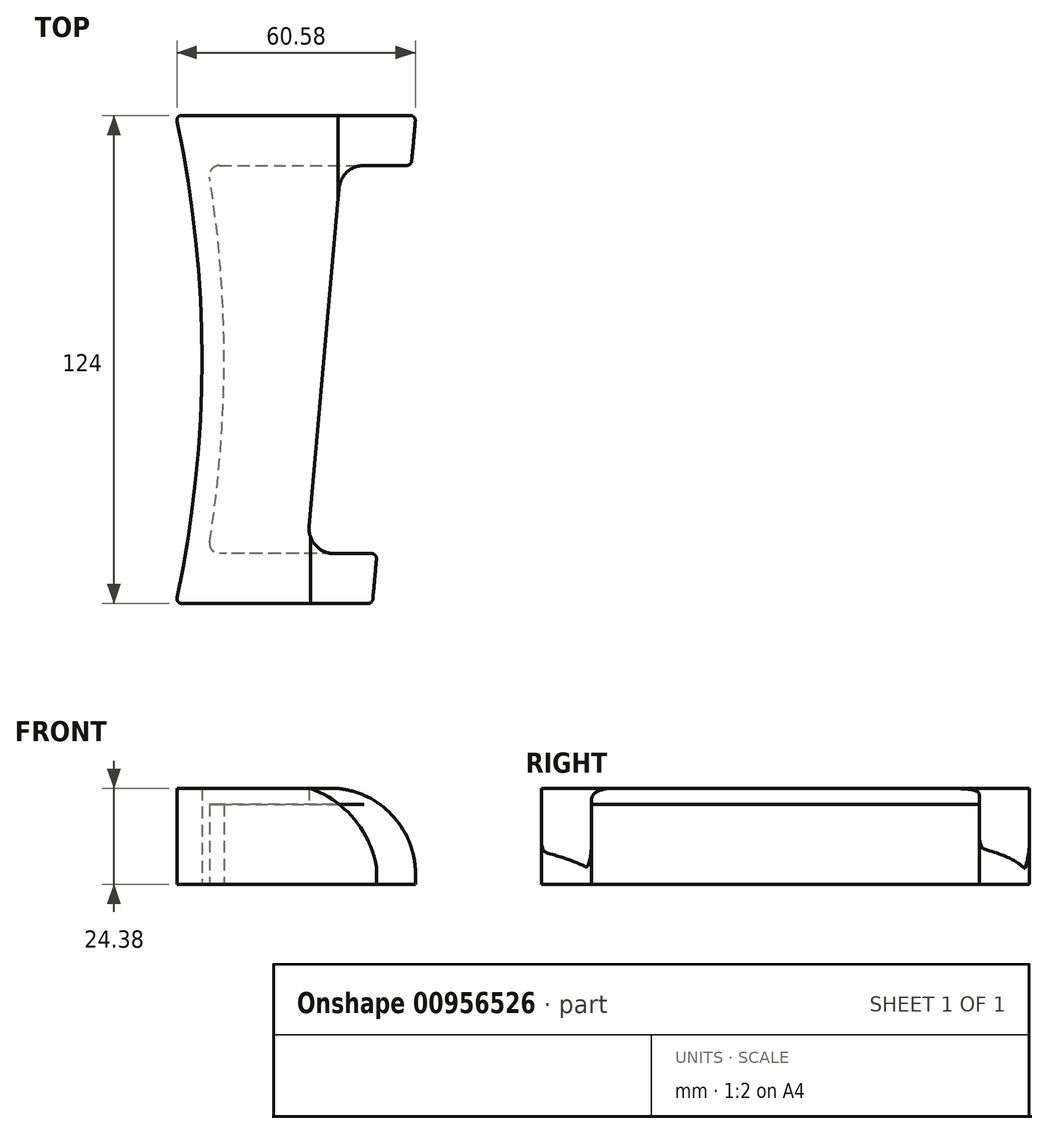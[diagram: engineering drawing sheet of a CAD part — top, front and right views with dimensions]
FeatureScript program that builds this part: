
annotation { "Feature Type Name" : "Feature", "Feature Type Description" : "" }
export const myFeature = defineFeature(function(context is Context, id is Id, definition is map)
    precondition{}
    {
        {
            var Q0;
            Q0=qCreatedBy(makeId("Top.planeOp"),FACE);
            var sketch = newSketch(context, id + "F0", { "sketchPlane" : qUnion([Q0])});
            skLineSegment(sketch, "E0", {"start": v(1.57, 0) * mm, "end": v(59.61, 0) * mm});
            skLineSegment(sketch, "E1", {"start": v(48.84, -124) * mm, "end": v(1.57, -124) * mm});
            skLineSegment(sketch, "E2", {"start": v(60.88, -1.38) * mm, "end": v(59.98, -11.54) * mm});
            skArc(sketch, "E3", {"start": v(0.33, -122.47) * mm, "mid": v(6.7, -62) * mm, "end": v(0.33, -1.53) * mm});
            skLineSegment(sketch, "E4.0", {"start": v(47.84, -12.7) * mm, "end": v(58.71, -12.7) * mm});
            skLineSegment(sketch, "E5.0", {"start": v(49.74, -111.3) * mm, "end": v(40.22, -111.3) * mm});
            skLineSegment(sketch, "E6.trimOffspring", {"start": v(41.51, -18.49) * mm, "end": v(33.89, -104.39) * mm});
            skLineSegment(sketch, "E7.trimOffspring", {"start": v(51, -112.68) * mm, "end": v(50.1, -122.84) * mm});
            skPoint(sketch, "E8.visualSharp", {"position": v(42.02, -12.7) * mm});
            skArc(sketch, "E8.filletArc", {"start": v(47.84, -12.7) * mm, "mid": v(43.55, -14.37) * mm, "end": v(41.51, -18.49) * mm});
            skPoint(sketch, "E9.visualSharp", {"position": v(33.28, -111.3) * mm});
            skArc(sketch, "E9.filletArc", {"start": v(33.89, -104.39) * mm, "mid": v(35.53, -109.24) * mm, "end": v(40.22, -111.3) * mm});
            skPoint(sketch, "E10.visualSharp", {"position": v(61, 0) * mm});
            skArc(sketch, "E10.filletArc", {"start": v(60.88, -1.38) * mm, "mid": v(60.55, -0.41) * mm, "end": v(59.61, 0) * mm});
            skPoint(sketch, "E11.visualSharp", {"position": v(59.87, -12.7) * mm});
            skArc(sketch, "E11.filletArc", {"start": v(58.71, -12.7) * mm, "mid": v(59.57, -12.37) * mm, "end": v(59.98, -11.54) * mm});
            skPoint(sketch, "E12.visualSharp", {"position": v(51.13, -111.3) * mm});
            skArc(sketch, "E12.filletArc", {"start": v(51, -112.68) * mm, "mid": v(50.68, -111.71) * mm, "end": v(49.74, -111.3) * mm});
            skPoint(sketch, "E13.visualSharp", {"position": v(50, -124) * mm});
            skArc(sketch, "E13.filletArc", {"start": v(48.84, -124) * mm, "mid": v(49.7, -123.67) * mm, "end": v(50.1, -122.84) * mm});
            skPoint(sketch, "E14.visualSharp", {"position": v(0, -124) * mm});
            skArc(sketch, "E14.filletArc", {"start": v(0.33, -122.47) * mm, "mid": v(0.59, -123.53) * mm, "end": v(1.57, -124) * mm});
            skPoint(sketch, "E15.visualSharp", {"position": v(0, 0) * mm});
            skArc(sketch, "E15.filletArc", {"start": v(1.57, 0) * mm, "mid": v(0.59, -0.47) * mm, "end": v(0.33, -1.53) * mm});
            skSolve(sketch);
        }
        {
            var Q0;
            Q0=makeQuery(id+"F0.imprint","IMPRINT",FACE,{"disambiguationData":[TD([[makeQuery(id+"F0.imprint","IMPRINT",EDGE,{"derivedFrom":sQuery(id+"F0.wireOp",EDGE,"E0")}),-1.0]])]});
            extrude(context, id + "F1", {"entities" : qUnion([Q0]), "depth" : 24.38 * mm, "offsetDistance" : 25.4 * mm});
        }
        {
            var Q0;
            Q0=makeQuery(id+"F1.opExtrude","CAP_FACE",FACE,{"disambiguationData":[OSD([sQuery(id+"F0.wireOp",EDGE,"E0"),sQuery(id+"F0.wireOp",EDGE,"E1"),sQuery(id+"F0.wireOp",EDGE,"E2"),sQuery(id+"F0.wireOp",EDGE,"E3"),sQuery(id+"F0.wireOp",EDGE,"E4.0"),sQuery(id+"F0.wireOp",EDGE,"E5.0"),sQuery(id+"F0.wireOp",EDGE,"E6.trimOffspring"),sQuery(id+"F0.wireOp",EDGE,"E7.trimOffspring"),sQuery(id+"F0.wireOp",EDGE,"E8.filletArc"),sQuery(id+"F0.wireOp",EDGE,"E9.filletArc"),sQuery(id+"F0.wireOp",EDGE,"E10.filletArc"),sQuery(id+"F0.wireOp",EDGE,"E11.filletArc"),sQuery(id+"F0.wireOp",EDGE,"E12.filletArc"),sQuery(id+"F0.wireOp",EDGE,"E13.filletArc"),sQuery(id+"F0.wireOp",EDGE,"E14.filletArc"),sQuery(id+"F0.wireOp",EDGE,"E15.filletArc")])],"isStart":true});
            var sketch = newSketch(context, id + "F2", { "sketchPlane" : qUnion([Q0])});
            skArc(sketch, "E16.0", {"start": v(8.63, 108.36) * mm, "mid": v(12.29, 62) * mm, "end": v(8.63, 15.64) * mm});
            skLineSegment(sketch, "E17.0", {"start": v(48.84, 111.3) * mm, "end": v(11.14, 111.3) * mm});
            skLineSegment(sketch, "E18.0", {"start": v(11.14, 12.7) * mm, "end": v(59.61, 12.7) * mm});
            skLineSegment(sketch, "E19", {"start": v(48.84, 111.3) * mm, "end": v(59.61, 12.7) * mm});
            skPoint(sketch, "E20.visualSharp", {"position": v(8.15, 111.3) * mm});
            skArc(sketch, "E20.filletArc", {"start": v(11.14, 111.3) * mm, "mid": v(9.2, 110.4) * mm, "end": v(8.63, 108.36) * mm});
            skPoint(sketch, "E21.visualSharp", {"position": v(8.15, 12.7) * mm});
            skArc(sketch, "E21.filletArc", {"start": v(8.63, 15.64) * mm, "mid": v(9.2, 13.6) * mm, "end": v(11.14, 12.7) * mm});
            skSolve(sketch);
        }
        {
            var Q0;
            Q0 = qSketchRegion(id + "F2", true);
            extrude(context, id + "F3", {"entities" : qUnion([Q0]), "operationType" : NewBodyOperationType.REMOVE, "oppositeDirection" : true, "depth" : 20.32 * mm, "offsetDistance" : 25.4 * mm});
        }
        {
            var Q0;
            Q0=makeQuery(id+"F1.opExtrude","SWEPT_FACE",FACE,{"disambiguationData":[OSD([sQuery(id+"F0.wireOp",EDGE,"E0")])]});
            var sketch = newSketch(context, id + "F4", { "sketchPlane" : qUnion([Q0])});
            skLineSegment(sketch, "E22", {"start": v(-60.9, 1.6) * mm, "end": v(-60.9, 0) * mm});
            skArc(sketch, "E23", {"start": v(-41.28, 24.38) * mm, "mid": v(-55.62, 16.9) * mm, "end": v(-60.9, 1.6) * mm});
            skLineSegment(sketch, "E24", {"start": v(-41.28, 24.38) * mm, "end": v(-40.57, 44.53) * mm});
            skLineSegment(sketch, "E25", {"start": v(-40.57, 44.53) * mm, "end": v(-74, 45.7) * mm});
            skLineSegment(sketch, "E26", {"start": v(-74, 45.7) * mm, "end": v(-79.64, 1.06) * mm});
            skLineSegment(sketch, "E27", {"start": v(-79.64, 1.06) * mm, "end": v(-60.9, 0) * mm});
            skSolve(sketch);
        }
        {
            var Q0;
            Q0=makeQuery(id+"F1.opExtrude","SWEPT_FACE",FACE,{"disambiguationData":[OSD([sQuery(id+"F0.wireOp",EDGE,"E1")])]});
            var sketch = newSketch(context, id + "F5", { "sketchPlane" : qUnion([Q0])});
            skArc(sketch, "E28", {"start": v(51.4, 0) * mm, "mid": v(46.67, 14.92) * mm, "end": v(34.2, 24.38) * mm});
            skLineSegment(sketch, "E29", {"start": v(34.2, 24.38) * mm, "end": v(51.4, 24.38) * mm});
            skLineSegment(sketch, "E30", {"start": v(51.4, 24.38) * mm, "end": v(51.4, 0) * mm});
            skSolve(sketch);
        }
        {
            var Q0;
            Q0 = qSketchRegion(id + "F4", true);
            extrude(context, id + "F6", {"entities" : qUnion([Q0]), "operationType" : NewBodyOperationType.REMOVE, "endBound" : BoundingType.THROUGH_ALL, "oppositeDirection" : true, "depth" : 25.4 * mm, "offsetDistance" : 25.4 * mm});
        }
        {
            var Q0;
            Q0 = qSketchRegion(id + "F5", true);
            extrude(context, id + "F7", {"entities" : qUnion([Q0]), "operationType" : NewBodyOperationType.REMOVE, "oppositeDirection" : true, "depth" : 19.5 * mm, "offsetDistance" : 25.4 * mm});
        }
    });
